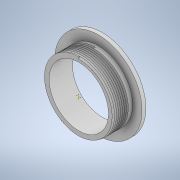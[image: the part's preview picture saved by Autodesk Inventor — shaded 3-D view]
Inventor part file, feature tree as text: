
AUTODESK INVENTOR PART (.ipt)
format: ipt  version: 2022.2 (Build 262287030, 287C)  size: 273,408 bytes
history: native  units: in
note: dims shown in document units (in); Inventor stores cm internally (conversion verified against a paired STEP export)
features: sketch x4, extrude x2, plane x1, helix x1
ambient origin geometry x8: Origin, YZ Plane, XZ Plane, XY Plane, X Axis, Y Axis, Z Axis, Center Point
bodies: Solid1 (feature_tree)
feature tree (8):
  extrude  "Extrusion1"  Depth=1.7614in
  extrude  "Extrusion2"  Depth=1.3831in
  sketch  "Sketch3"  dims[d7=0.0in]
  plane  "Work Plane1"
  helix  "Coil1"  [1 undecoded]
  sketch  "Sketch1"  dims[d0=1.1969in d1=1.7614in]
  sketch  "Sketch2"  dims[d2=0.0787in d3=0.0in d4=1.3831in d5=0.3937in d6=0.0in]
  sketch  "Sketch4"  dims[d8=0.0in d9=0.0in d10=0.0394in d11=0.0394in d12=0.3937in d13=3.1496in d14=0.0in d15=90.0deg d16=90.0deg d17=0.0in d18=0.0in]
note: 1 required parameter value undecoded (feature->parameter linkage not recoverable at this tier; creation-order binding heuristic only, values carry confidence <= 0.55)
